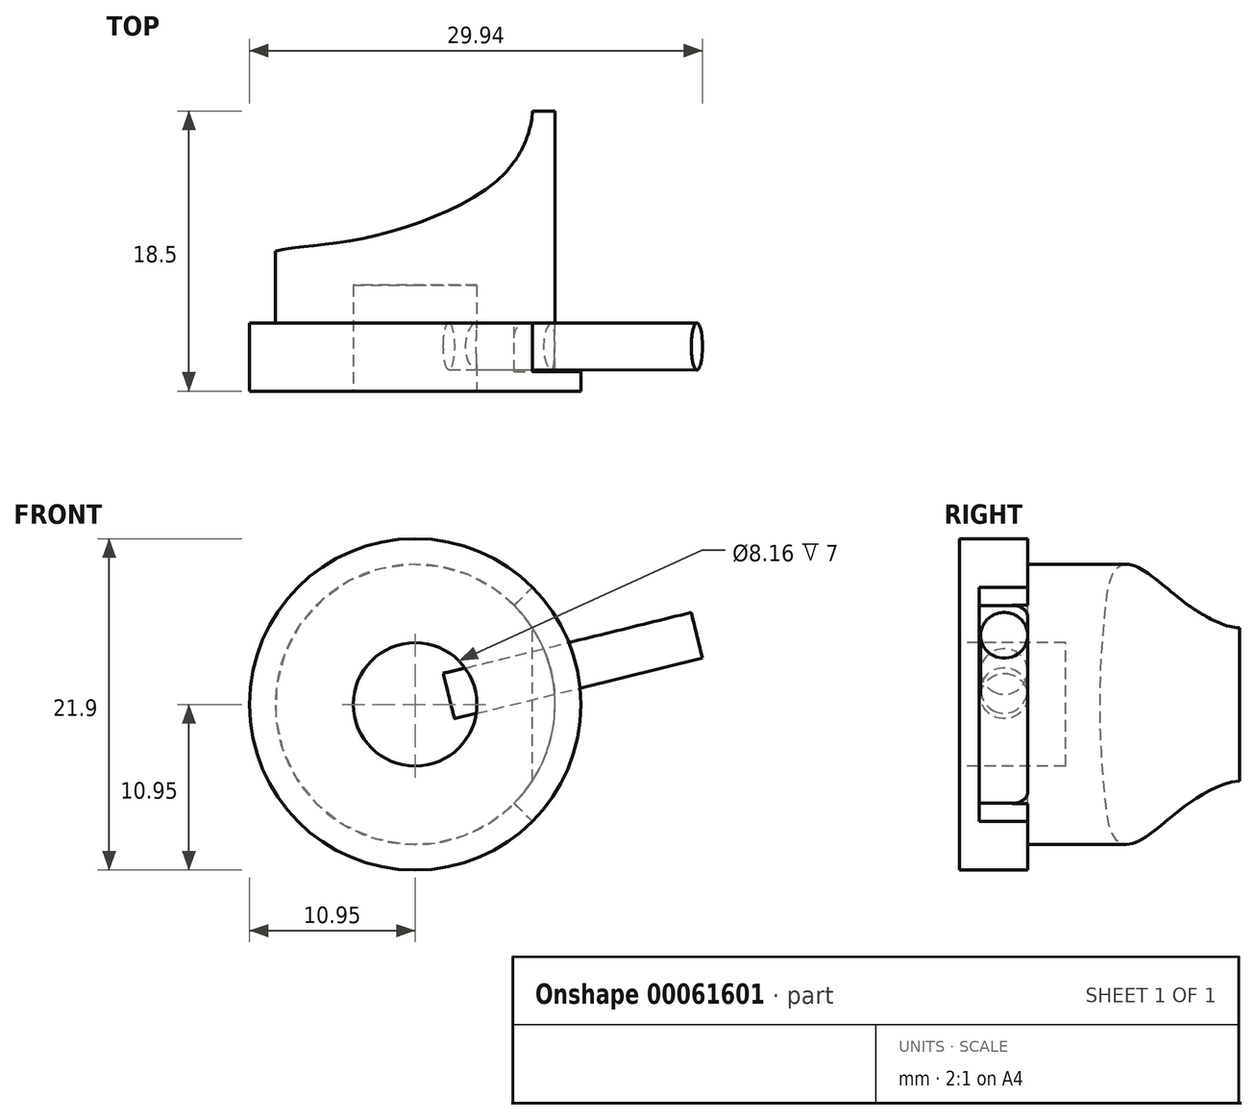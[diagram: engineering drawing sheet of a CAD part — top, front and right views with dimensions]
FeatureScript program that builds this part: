
annotation { "Feature Type Name" : "Feature", "Feature Type Description" : "" }
export const myFeature = defineFeature(function(context is Context, id is Id, definition is map)
    precondition{}
    {
        {
            var Q0;
            Q0=qCreatedBy(makeId("Top.planeOp"),FACE);
            var sketch = newSketch(context, id + "F0", { "sketchPlane" : qUnion([Q0])});
            skCircle(sketch, "E0", {"center": v(0, 0) * mm, "radius": 9.25 * mm, "construction": true});
            skLineSegment(sketch, "E1.rect.bottom", {"start": v(10.95, 30) * mm, "end": v(-10.95, 30) * mm, "construction": true});
            skLineSegment(sketch, "E1.rect.top", {"start": v(10.95, -30) * mm, "end": v(-10.95, -30) * mm, "construction": true});
            skLineSegment(sketch, "E1.rect.left", {"start": v(10.95, 30) * mm, "end": v(10.95, -30) * mm, "construction": true});
            skLineSegment(sketch, "E1.rect.right", {"start": v(-10.95, 30) * mm, "end": v(-10.95, -30) * mm, "construction": true});
            skLineSegment(sketch, "E2", {"start": v(-10.95, -14) * mm, "end": v(10.95, -14) * mm, "construction": true});
            skLineSegment(sketch, "E3", {"start": v(-10.95, 14) * mm, "end": v(10.95, 14) * mm, "construction": true});
            skSolve(sketch);
        }
        {
            var Q0;
            Q0=qCreatedBy(makeId("Top.planeOp"),FACE);
            var sketch = newSketch(context, id + "F1", { "sketchPlane" : qUnion([Q0])});
            skCircle(sketch, "E4.0", {"center": v(0, 0) * mm, "radius": 9.25 * mm, "construction": true});
            skLineSegment(sketch, "E5.0", {"start": v(-10.95, -14) * mm, "end": v(10.95, -14) * mm, "construction": true});
            skLineSegment(sketch, "E6.0", {"start": v(10.95, -30) * mm, "end": v(-10.95, -30) * mm, "construction": true});
            skLineSegment(sketch, "E7.0", {"start": v(10.95, 30) * mm, "end": v(10.95, -30) * mm, "construction": true});
            skLineSegment(sketch, "E8.0", {"start": v(-10.95, 30) * mm, "end": v(-10.95, -30) * mm, "construction": true});
            skLineSegment(sketch, "E9", {"start": v(9.25, 0) * mm, "end": v(9.25, -14) * mm});
            skLineSegment(sketch, "E10", {"start": v(9.25, 0) * mm, "end": v(0, 0) * mm});
            skLineSegment(sketch, "E11", {"start": v(0, 0) * mm, "end": v(0, -18.5) * mm});
            skPoint(sketch, "E11.endSnap0", {"position": v(0, -14) * mm});
            skLineSegment(sketch, "E12", {"start": v(0, -18.5) * mm, "end": v(10.95, -18.5) * mm});
            skLineSegment(sketch, "E13", {"start": v(9.25, -14) * mm, "end": v(9.25, -17.1) * mm, "construction": true});
            skLineSegment(sketch, "E14", {"start": v(9.25, -17.1) * mm, "end": v(10.95, -17.1) * mm, "construction": true});
            skLineSegment(sketch, "E15", {"start": v(9.25, -15.55) * mm, "end": v(0, -15.55) * mm, "construction": true});
            skLineSegment(sketch, "E16", {"start": v(9.25, -14) * mm, "end": v(10.95, -14) * mm});
            skLineSegment(sketch, "E17", {"start": v(10.95, -14) * mm, "end": v(10.95, -18.5) * mm});
            skSolve(sketch);
        }
        {
            var Q0;
            Q0 = qSketchRegion(id + "F1", true);
            var Q1;
            Q1=sQuery(id+"F1.wireOp",EDGE,"E11");
            revolve(context, id + "F2", {"entities" : qUnion([Q0]), "axis" : qUnion([Q1]), "revolveType" : RevolveType.FULL});
        }
        {
            var Q0;
            Q0=qCreatedBy(makeId("Top.planeOp"),FACE);
            var sketch = newSketch(context, id + "F3", { "sketchPlane" : qUnion([Q0])});
            skCircle(sketch, "E18.0", {"center": v(0, 0) * mm, "radius": 9.25 * mm, "construction": true});
            skLineSegment(sketch, "E19.0", {"start": v(-10.95, -14) * mm, "end": v(10.95, -14) * mm, "construction": true});
            skLineSegment(sketch, "E20", {"start": v(9.25, 0) * mm, "end": v(7.75, 0) * mm});
            skLineSegment(sketch, "E21", {"start": v(-9.25, 0) * mm, "end": v(-9.25, -9.25) * mm, "construction": true});
            skLineSegment(sketch, "E22", {"start": v(0, -9.25) * mm, "end": v(-9.25, -9.25) * mm, "construction": true});
            skFitSpline(sketch, "E23", {"points": [v(7.75, 0) * mm, v(6.86, -2.86) * mm, v(3.63, -5.84) * mm, v(-3.7, -8.47) * mm, v(-9.25, -9.25) * mm], "startDerivative": vector(-0.5, -13.38) * mm, "endDerivative": vector(-20.98, -4.23) * mm});
            skLineSegment(sketch, "E24", {"start": v(-9.25, -9.25) * mm, "end": v(-9.25, 10.52) * mm});
            skLineSegment(sketch, "E25", {"start": v(-9.25, 10.52) * mm, "end": v(9.25, 10.52) * mm});
            skLineSegment(sketch, "E26", {"start": v(9.25, 10.52) * mm, "end": v(9.25, 0) * mm});
            skSolve(sketch);
        }
        {
            var Q0;
            Q0 = qSketchRegion(id + "F3", true);
            extrude(context, id + "F4", {"entities" : qUnion([Q0]), "operationType" : NewBodyOperationType.REMOVE, "endBound" : BoundingType.THROUGH_ALL, "oppositeDirection" : true, "depth" : 25 * mm, "hasSecondDirection" : true, "secondDirectionBound" : SecondDirectionBoundingType.THROUGH_ALL, "secondDirectionOppositeDirection" : false, "secondDirectionDepth" : 25 * mm});
        }
        {
            var Q0;
            Q0=makeQuery(id+"F2.opRevolve","SWEPT_FACE",FACE,{"disambiguationData":[OSD([sQuery(id+"F1.wireOp",EDGE,"E12")])]});
            var sketch = newSketch(context, id + "F5", { "sketchPlane" : qUnion([Q0])});
            skCircle(sketch, "E27", {"center": v(0, 0) * mm, "radius": 4.08 * mm});
            skSolve(sketch);
        }
        {
            var Q0;
            Q0 = qSketchRegion(id + "F5", true);
            extrude(context, id + "F6", {"entities" : qUnion([Q0]), "operationType" : NewBodyOperationType.REMOVE, "oppositeDirection" : true, "depth" : 7 * mm});
        }
        {
            var Q0;
            Q0=makeQuery(id+"F2.opRevolve","SWEPT_FACE",FACE,{"disambiguationData":[OSD([sQuery(id+"F1.wireOp",EDGE,"E16")])]});
            var sketch = newSketch(context, id + "F7", { "sketchPlane" : qUnion([Q0])});
            skCircle(sketch, "E28.0", {"center": v(0, 0) * mm, "radius": 10.95 * mm, "construction": true});
            skLineSegment(sketch, "E29", {"start": v(0, 0) * mm, "end": v(-7.74, 7.74) * mm, "construction": true});
            skLineSegment(sketch, "E30", {"start": v(0, 0) * mm, "end": v(-7.74, -7.74) * mm, "construction": true});
            skArc(sketch, "E31", {"start": v(-6.54, 6.54) * mm, "mid": v(-9.25, 0) * mm, "end": v(-6.54, -6.54) * mm});
            skArc(sketch, "E32", {"start": v(-7.74, 7.74) * mm, "mid": v(-10.95, 0) * mm, "end": v(-7.74, -7.74) * mm});
            skLineSegment(sketch, "E33", {"start": v(-6.54, 6.54) * mm, "end": v(-7.74, 7.74) * mm});
            skLineSegment(sketch, "E34", {"start": v(-6.54, -6.54) * mm, "end": v(-7.74, -7.74) * mm});
            skCircle(sketch, "E35.0", {"center": v(0, 0) * mm, "radius": 9.25 * mm, "construction": true});
            skSolve(sketch);
        }
        {
            var Q0;
            Q0 = qSketchRegion(id + "F7", true);
            extrude(context, id + "F8", {"entities" : qUnion([Q0]), "operationType" : NewBodyOperationType.REMOVE, "oppositeDirection" : true, "depth" : 3.2 * mm});
        }
        {
            var Q0;
            Q0=sQuery(id+"F1.wireOp",VERTEX,"E15.start");
            var Q1;
            Q1=sQuery(id+"F1.wireOp",EDGE,"E13");
            cPlane(context, id + "F9", {"entities" : qUnion([Q0, Q1]), "cplaneType" : CPlaneType.LINE_POINT, "offset" : 150 * mm, "width" : 150 * mm, "height" : 150 * mm});
        }
        {
            var Q0;
            Q0=qCreatedBy(id+"F9.planeOp",FACE);
            var sketch = newSketch(context, id + "F10", { "sketchPlane" : qUnion([Q0])});
            skLineSegment(sketch, "E36", {"start": v(0, 0) * mm, "end": v(20.32, 8.17) * mm, "construction": true});
            skLineSegment(sketch, "E37", {"start": v(0, 0) * mm, "end": v(22.95, 2.26) * mm, "construction": true});
            skLineSegment(sketch, "E38", {"start": v(10.16, 4.08) * mm, "end": v(10.9, 1.07) * mm, "construction": true});
            skLineSegment(sketch, "E39", {"start": v(0, 0) * mm, "end": v(10.53, 2.58) * mm, "construction": true});
            skLineSegment(sketch, "E40.bottom", {"start": v(1.86, 2.05) * mm, "end": v(18.25, 6.07) * mm});
            skLineSegment(sketch, "E40.top", {"start": v(2.23, 0.55) * mm, "end": v(18.62, 4.56) * mm});
            skLineSegment(sketch, "E40.left", {"start": v(1.86, 2.05) * mm, "end": v(2.23, 0.55) * mm});
            skLineSegment(sketch, "E40.right", {"start": v(18.25, 6.07) * mm, "end": v(18.62, 4.56) * mm});
            skPoint(sketch, "E41", {"position": v(10.16, 4.08) * mm});
            skCircle(sketch, "E42.0", {"center": v(0, 0) * mm, "radius": 10.95 * mm, "construction": true});
            skSolve(sketch);
        }
        {
            var Q0;
            Q0 = qSketchRegion(id + "F10", true);
            var Q1;
            Q1=sQuery(id+"F10.wireOp",EDGE,"E40.top");
            revolve(context, id + "F11", {"entities" : qUnion([Q0]), "axis" : qUnion([Q1]), "revolveType" : RevolveType.FULL});
        }
        {
            var Q0;
            Q0=makeQuery(id+"F11.opRevolve","SWEPT_BODY",BODY,{"disambiguationData":[OSD([sQuery(id+"F10.wireOp",EDGE,"E40.bottom"),sQuery(id+"F10.wireOp",EDGE,"E40.top"),sQuery(id+"F10.wireOp",EDGE,"E40.left"),sQuery(id+"F10.wireOp",EDGE,"E40.right")])]});
            var Q1;
            Q1=makeQuery(id+"F2.opRevolve","SWEPT_BODY",BODY,{"disambiguationData":[OSD([sQuery(id+"F1.wireOp",EDGE,"E9"),sQuery(id+"F1.wireOp",EDGE,"E10"),sQuery(id+"F1.wireOp",EDGE,"E11"),sQuery(id+"F1.wireOp",EDGE,"E12"),sQuery(id+"F1.wireOp",EDGE,"AYjZyxld-uefS-yame-6VsP-UoN1xdjAYjeZ"),sQuery(id+"F1.wireOp",EDGE,"E13"),sQuery(id+"F1.wireOp",EDGE,"E14")])]});
            booleanBodies(context, id + "F12", {"operationType" : BooleanOperationType.SUBTRACTION, "tools" : qUnion([Q0]), "targets" : qUnion([Q1]), "keepTools" : true});
        }
        {
            var Q0;
            Q0=makeQuery(id+"F8.boolean.opBoolean","COPY",EDGE,{"derivedFrom":makeQuery(id+"F8.opExtrude","CAP_EDGE",EDGE,{"disambiguationData":[OSD([sQuery(id+"F7.wireOp",EDGE,"E33")])],"isStart":true})});
            var Q1;
            Q1=makeQuery(id+"F8.boolean.opBoolean","COPY",EDGE,{"derivedFrom":makeQuery(id+"F8.opExtrude","CAP_EDGE",EDGE,{"disambiguationData":[OSD([sQuery(id+"F7.wireOp",EDGE,"E34")])],"isStart":true})});
            fillet(context, id + "F13", {"entities" : qUnion([Q0, Q1]), "radius" : 1 * mm, "allowEdgeOverflow" : false});
        }
    });
